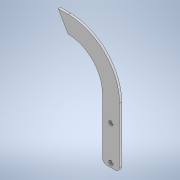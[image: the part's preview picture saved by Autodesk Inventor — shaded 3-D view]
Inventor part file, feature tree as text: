
AUTODESK INVENTOR PART (.ipt)
format: ipt  version: 2022 (Build 260153000, 153)  size: 123,392 bytes
history: native  units: mm
features: extrude x2, sketch x1
ambient origin geometry x8: Origin, YZ Plane, XZ Plane, XY Plane, X Axis, Y Axis, Z Axis, Center Point
bodies: Solid1 (feature_tree)
feature tree (3):
  extrude  "Extrusion1"  Depth=5.0mm TaperAngle=0.0deg
  extrude  "Extrusion3"  Depth=80.0mm
  sketch  "Sketch3"  dims[d1=40.0mm d3=5.0mm d4=0.0mm d11=80.0mm d12=140.0mm d13=10.0mm d14=10.0mm d15=10.0mm d16=80.0mm d17=10.0mm d18=0.0mm d19=120.0deg]
